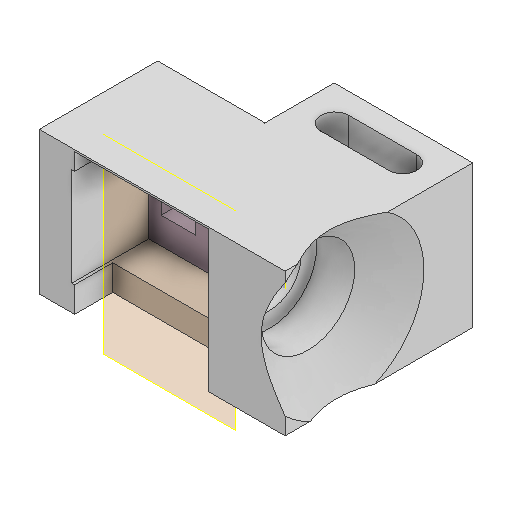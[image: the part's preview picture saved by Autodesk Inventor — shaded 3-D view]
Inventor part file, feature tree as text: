
AUTODESK INVENTOR PART (.ipt)
format: ipt  version: 2022 (Build 260153000, 153)  size: 225,792 bytes
history: native  units: mm
features: other x7, extrude x6, sketch x6, reference x5, plane x3, projected_geometry x3, chamfer x2
ambient origin geometry x8: Origin, YZ Plane, XZ Plane, XY Plane, X Axis, Y Axis, Z Axis, Center Point
bodies: Volumenkörper1 (feature_tree)
feature tree (32):
  plane  "Arbeitsebene1"
  plane  "Arbeitsebene2"
  extrude  "Extrusion1"  Depth=3.0mm
  sketch  "Skizze2"  dims[d2=4.0mm d3=12.0mm]
  plane  "Arbeitsebene3"
  extrude  "Extrusion2"  Depth=4.0mm
  extrude  "Extrusion3"  Depth=6.0mm
  extrude  "Extrusion4"  Depth=4.0mm
  extrude  "Extrusion5"  Depth=10.5mm TaperAngle=0.0deg
  extrude  "Extrusion6"  Depth=6.0mm TaperAngle=0.0deg
  chamfer  "Fase1"  Distance=20.0mm
  chamfer  "Fase2"  Distance=10.0mm
  sketch  "Skizze1"  dims[d0=5.0mm d1=3.0mm]
  reference  "Referenz1"
  reference  "Referenz2"
  projected_geometry  "Projizierte Kontur1"
  sketch  "Skizze3"  dims[d4=6.0mm d5=0.0mm d6=0.3mm]
  reference  "Referenz3"
  projected_geometry  "Projizierte Kontur2"
  sketch  "Skizze4"  dims[d7=4.0mm d8=0.0mm d9=1.0mm]
  reference  "Referenz5"
  sketch  "Skizze5"  dims[d10=5.5mm d11=0.0mm d13=10.5mm d14=0.0mm]
  reference  "Referenz6"
  sketch  "Skizze6"  dims[d15=4.0mm d16=0.0mm d17=6.0mm d18=0.0mm d19=20.0mm d20=10.0mm d21=4.0mm d22=5.5mm d23=0.0mm d24=5.0mm d25=2.0mm d26=45.0deg d27=4.0mm d28=2.0mm d29=45.0deg d30=13.5mm]
  projected_geometry  "Projizierte Kontur3"
  other  "<userpath>\Documents\GitHub\Guinardia\INVENTOR\Assemlby_Scanner_v0.iam"
  other  "Assemlby_Scanner_v0.iam"
  other  "Assembly_Huawei_P30_Scanninglens:1"
  other  "00_huawei_p30_Objectivelensassembly:1"
  other  "00_Huawei_P30_Lens_Adapterpcb:1"
  other  "00_SMAConnector_fiber copy:1"
  other  "Baugruppe1"
